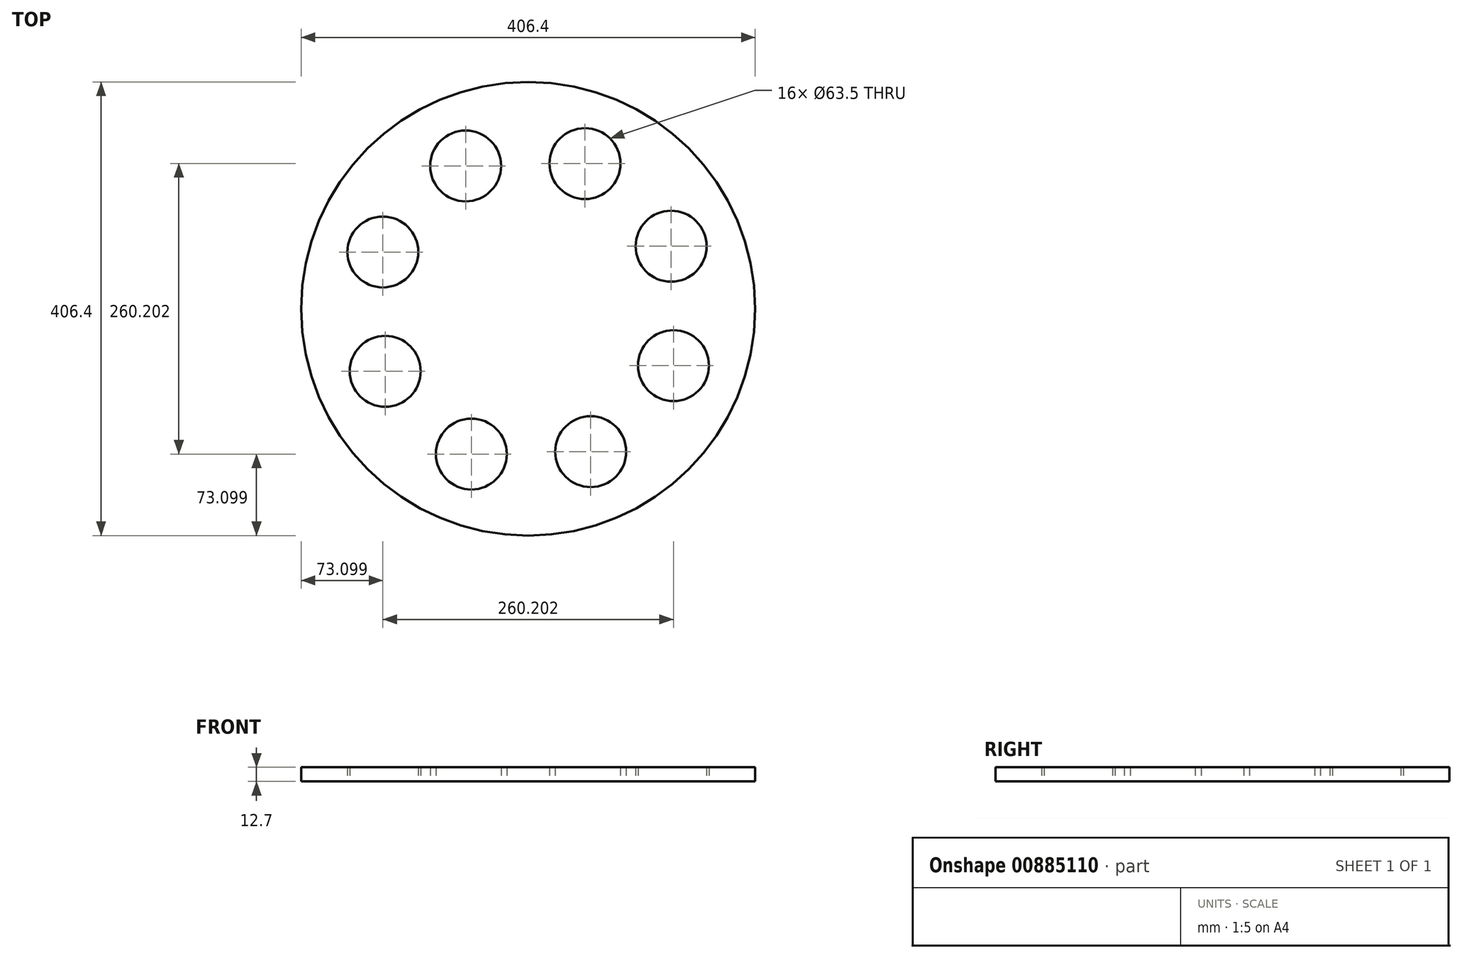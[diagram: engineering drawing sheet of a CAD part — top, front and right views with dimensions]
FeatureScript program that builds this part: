
annotation { "Feature Type Name" : "Feature", "Feature Type Description" : "" }
export const myFeature = defineFeature(function(context is Context, id is Id, definition is map)
    precondition{}
    {
        {
            var Q0;
            Q0=qCreatedBy(makeId("Top.planeOp"),FACE);
            var sketch = newSketch(context, id + "F0", { "sketchPlane" : qUnion([Q0])});
            skCircle(sketch, "E0", {"center": v(0, 0) * mm, "radius": 190.5 * mm, "construction": true});
            skCircle(sketch, "E1", {"center": v(-56.01, 127.98) * mm, "radius": 50.8 * mm, "construction": true});
            skCircle(sketch, "E2.1.0", {"center": v(-130.1, 50.9) * mm, "radius": 50.8 * mm, "construction": true});
            skCircle(sketch, "E2.2.0", {"center": v(-127.98, -56.01) * mm, "radius": 50.8 * mm, "construction": true});
            skCircle(sketch, "E2.3.0", {"center": v(-50.9, -130.1) * mm, "radius": 50.8 * mm, "construction": true});
            skCircle(sketch, "E2.4.0", {"center": v(56.01, -127.98) * mm, "radius": 50.8 * mm, "construction": true});
            skCircle(sketch, "E2.5.0", {"center": v(130.1, -50.9) * mm, "radius": 50.8 * mm, "construction": true});
            skCircle(sketch, "E3.1.6.0", {"center": v(127.98, 56.01) * mm, "radius": 50.8 * mm, "construction": true});
            skCircle(sketch, "E3.1.7.0", {"center": v(50.9, 130.1) * mm, "radius": 50.8 * mm, "construction": true});
            skCircle(sketch, "E4", {"center": v(0, 0) * mm, "radius": 203.2 * mm});
            skCircle(sketch, "E5", {"center": v(-56.01, 127.98) * mm, "radius": 31.75 * mm});
            skCircle(sketch, "E6.1.0", {"center": v(-130.1, 50.9) * mm, "radius": 31.75 * mm});
            skCircle(sketch, "E6.2.0", {"center": v(-127.98, -56.01) * mm, "radius": 31.75 * mm});
            skCircle(sketch, "E6.3.0", {"center": v(-50.9, -130.1) * mm, "radius": 31.75 * mm});
            skCircle(sketch, "E6.4.0", {"center": v(56.01, -127.98) * mm, "radius": 31.75 * mm});
            skCircle(sketch, "E6.5.0", {"center": v(130.1, -50.9) * mm, "radius": 31.75 * mm});
            skCircle(sketch, "E6.6.0", {"center": v(127.98, 56.01) * mm, "radius": 31.75 * mm});
            skCircle(sketch, "E6.7.0", {"center": v(50.9, 130.1) * mm, "radius": 31.75 * mm});
            skSolve(sketch);
        }
        {
            var Q0;
            Q0 = qSketchRegion(id + "F0", true);
            extrude(context, id + "F1", {"entities" : qUnion([Q0]), "depth" : 12.7 * mm, "offsetDistance" : 25.4 * mm});
        }
    });
